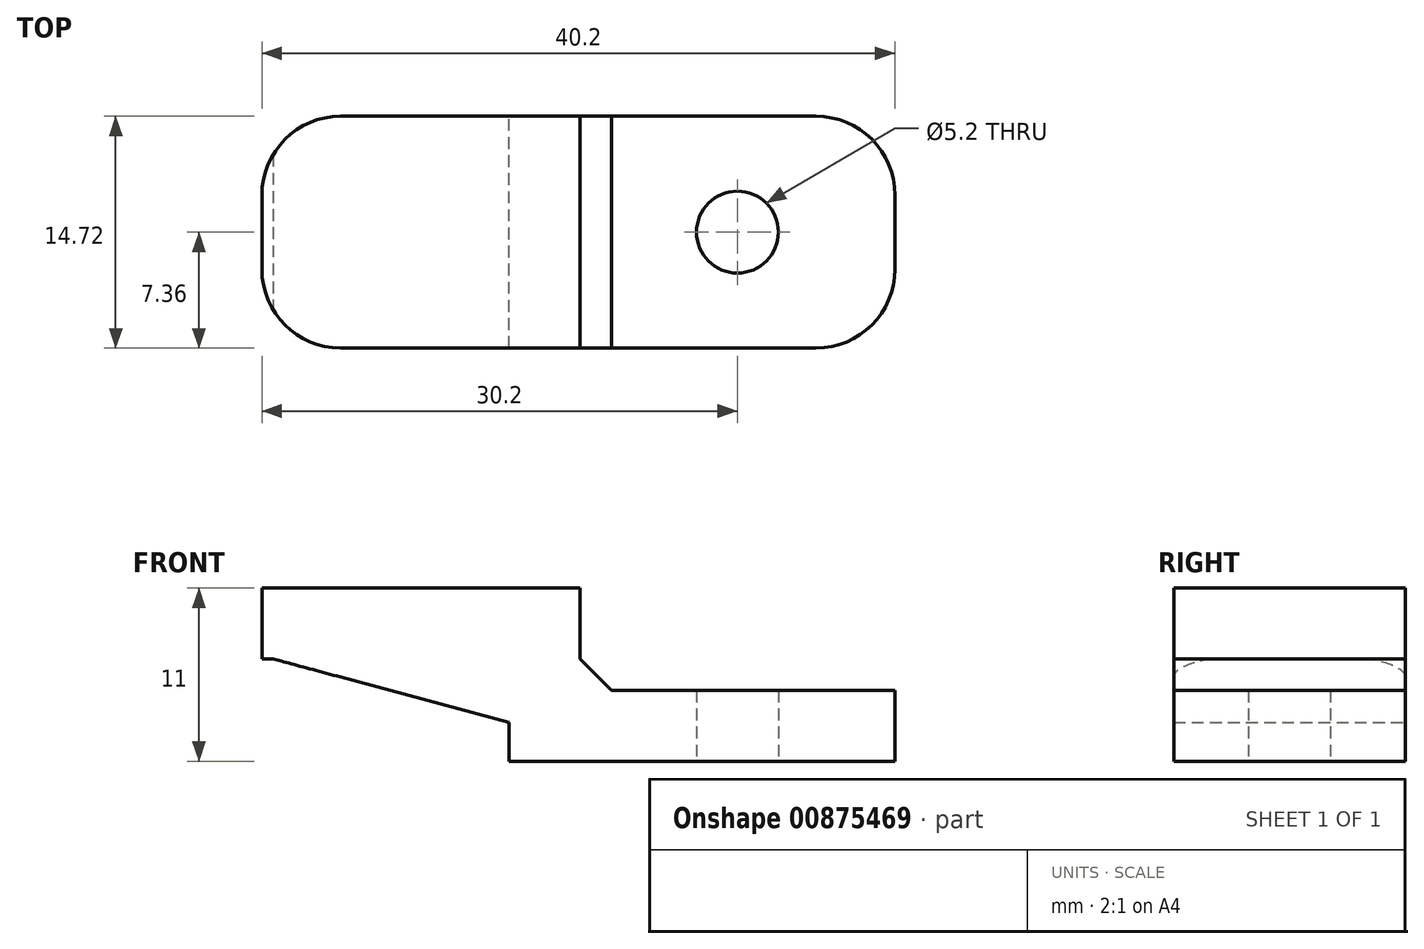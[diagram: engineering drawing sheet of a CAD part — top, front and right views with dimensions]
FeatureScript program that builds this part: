
annotation { "Feature Type Name" : "Feature", "Feature Type Description" : "" }
export const myFeature = defineFeature(function(context is Context, id is Id, definition is map)
    precondition{}
    {
        {
            var Q0;
            Q0=qCreatedBy(makeId("Front.planeOp"),FACE);
            var sketch = newSketch(context, id + "F0", { "sketchPlane" : qUnion([Q0])});
            skLineSegment(sketch, "E0.bottom", {"start": v(0, 0) * mm, "end": v(24.5, 0) * mm});
            skLineSegment(sketch, "E0.top", {"start": v(0, -4.5) * mm, "end": v(24.5, -4.5) * mm});
            skLineSegment(sketch, "E0.left", {"start": v(0, 0) * mm, "end": v(0, -4.5) * mm});
            skLineSegment(sketch, "E0.right", {"start": v(24.5, 0) * mm, "end": v(24.5, -4.5) * mm});
            skLineSegment(sketch, "E1.bottom", {"start": v(0, -4.5) * mm, "end": v(4.5, -4.5) * mm});
            skLineSegment(sketch, "E1.top", {"start": v(0, 2) * mm, "end": v(4.5, 2) * mm});
            skLineSegment(sketch, "E1.left", {"start": v(0, -4.5) * mm, "end": v(0, 2) * mm});
            skLineSegment(sketch, "E1.right", {"start": v(4.5, -4.5) * mm, "end": v(4.5, 2) * mm});
            skLineSegment(sketch, "E2.bottom", {"start": v(4.5, 2) * mm, "end": v(-15.7, 2) * mm});
            skLineSegment(sketch, "E2.top", {"start": v(4.5, 6.5) * mm, "end": v(-15.7, 6.5) * mm});
            skLineSegment(sketch, "E2.left", {"start": v(4.5, 2) * mm, "end": v(4.5, 6.5) * mm});
            skLineSegment(sketch, "E2.right", {"start": v(-15.7, 2) * mm, "end": v(-15.7, 6.5) * mm});
            skSolve(sketch);
        }
        {
            var Q0;
            Q0 = qSketchRegion(id + "F0", true);
            extrude(context, id + "F1", {"entities" : qUnion([Q0]), "endBound" : BoundingType.SYMMETRIC, "depth" : 14.72 * mm, "offsetDistance" : 25 * mm});
        }
        {
            var Q0;
            Q0=makeQuery(id+"F1.opExtrude","SWEPT_FACE",FACE,{"disambiguationData":[OSD([sQuery(id+"F0.wireOp",EDGE,"E0.bottom")])]});
            var sketch = newSketch(context, id + "F2", { "sketchPlane" : qUnion([Q0])});
            skCircle(sketch, "E3", {"center": v(14.5, 0) * mm, "radius": 2.6 * mm});
            skPoint(sketch, "E3.centerSnap0", {"position": v(24.5, 0) * mm});
            skPoint(sketch, "E3.centerSnap1", {"position": v(14.5, -7.36) * mm});
            skCircle(sketch, "E4", {"center": v(-5.6, 0) * mm, "radius": 2.6 * mm, "construction": true});
            skSolve(sketch);
        }
        {
            var Q0;
            Q0 = qSketchRegion(id + "F2", true);
            extrude(context, id + "F3", {"entities" : qUnion([Q0]), "operationType" : NewBodyOperationType.REMOVE, "endBound" : BoundingType.SYMMETRIC, "depth" : 100 * mm, "offsetDistance" : 25 * mm});
        }
        {
            var Q0;
            Q0=makeQuery(id+"F1.opExtrude","SWEPT_EDGE",EDGE,{"disambiguationData":[OSD([sQuery(id+"F0.wireOp",EDGE,"E1.left"),sQuery(id+"F0.wireOp",EDGE,"E2.bottom")])]});
            chamfer(context, id + "F4", {"entities" : qUnion([Q0]), "chamferType" : ChamferType.OFFSET_ANGLE, "width" : 15 * mm, "oppositeDirection" : true, "angle" : 15 * degree, "tangentPropagation" : true});
        }
        {
            var Q0;
            Q0=makeQuery(id+"F1.opExtrude","CAP_EDGE",EDGE,{"disambiguationData":[OSD([sQuery(id+"F0.wireOp",EDGE,"E2.right")])],"isStart":true});
            var Q1;
            Q1=makeQuery(id+"F1.opExtrude","CAP_EDGE",EDGE,{"disambiguationData":[OSD([sQuery(id+"F0.wireOp",EDGE,"E2.right")])],"isStart":false});
            var Q2;
            Q2=makeQuery(id+"F1.opExtrude","CAP_EDGE",EDGE,{"disambiguationData":[OSD([sQuery(id+"F0.wireOp",EDGE,"E0.right")])],"isStart":true});
            var Q3;
            Q3=makeQuery(id+"F1.opExtrude","CAP_EDGE",EDGE,{"disambiguationData":[OSD([sQuery(id+"F0.wireOp",EDGE,"E0.right")])],"isStart":false});
            fillet(context, id + "F5", {"entities" : qUnion([Q0, Q1, Q2, Q3]), "radius" : 5 * mm, "tangentPropagation" : true, "allowEdgeOverflow" : false});
        }
        {
            var Q0;
            Q0=makeQuery(id+"F1.opExtrude","SWEPT_EDGE",EDGE,{"disambiguationData":[OSD([sQuery(id+"F0.wireOp",EDGE,"E0.bottom"),sQuery(id+"F0.wireOp",EDGE,"E1.right")])]});
            chamfer(context, id + "F6", {"entities" : qUnion([Q0]), "width" : 2 * mm, "tangentPropagation" : true});
        }
    });
